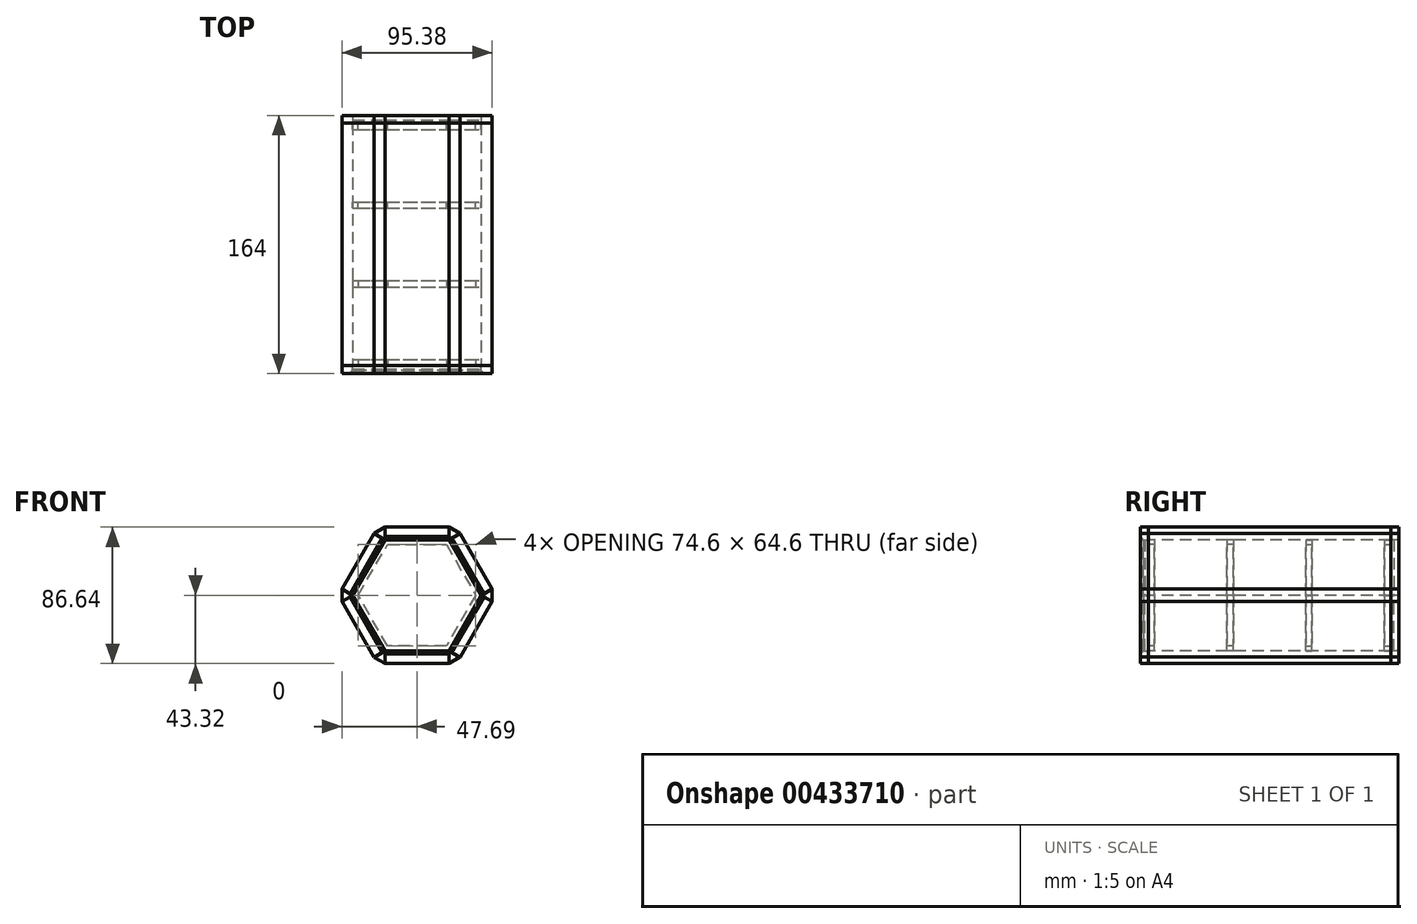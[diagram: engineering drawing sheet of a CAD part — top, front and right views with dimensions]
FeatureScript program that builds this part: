
annotation { "Feature Type Name" : "Feature", "Feature Type Description" : "" }
export const myFeature = defineFeature(function(context is Context, id is Id, definition is map)
    precondition{}
    {
        {
            var Q0;
            Q0=qCreatedBy(makeId("Front.planeOp"),FACE);
            var sketch = newSketch(context, id + "F0", { "sketchPlane" : qUnion([Q0])});
            skCircle(sketch, "E0.cCircle", {"center": v(0, 0) * mm, "radius": 43.3 * mm, "construction": true});
            skLineSegment(sketch, "E0.0", {"start": v(-50, 0) * mm, "end": v(-25, 43.3) * mm});
            skLineSegment(sketch, "E0.1", {"start": v(-25, 43.3) * mm, "end": v(25, 43.3) * mm});
            skLineSegment(sketch, "E0.2", {"start": v(25, 43.3) * mm, "end": v(50, 0) * mm});
            skLineSegment(sketch, "E0.3", {"start": v(50, 0) * mm, "end": v(25, -43.3) * mm});
            skLineSegment(sketch, "E0.4", {"start": v(25, -43.3) * mm, "end": v(-25, -43.3) * mm});
            skLineSegment(sketch, "E0.5", {"start": v(-25, -43.3) * mm, "end": v(-50, 0) * mm});
            skPoint(sketch, "E0.0.midPoint", {"position": v(-37.5, 21.65) * mm});
            skLineSegment(sketch, "E1.0", {"start": v(-20.38, 35.3) * mm, "end": v(20.38, 35.3) * mm});
            skLineSegment(sketch, "E1.1", {"start": v(40.76, 0) * mm, "end": v(20.38, -35.3) * mm});
            skLineSegment(sketch, "E1.2", {"start": v(20.38, -35.3) * mm, "end": v(-20.38, -35.3) * mm});
            skLineSegment(sketch, "E1.3", {"start": v(20.38, 35.3) * mm, "end": v(40.76, 0) * mm});
            skLineSegment(sketch, "E1.4", {"start": v(-20.38, -35.3) * mm, "end": v(-40.76, 0) * mm});
            skLineSegment(sketch, "E1.5", {"start": v(-40.76, 0) * mm, "end": v(-20.38, 35.3) * mm});
            skLineSegment(sketch, "E2.0", {"start": v(-37.3, 0) * mm, "end": v(-18.65, 32.3) * mm});
            skLineSegment(sketch, "E2.1", {"start": v(18.65, 32.3) * mm, "end": v(37.3, 0) * mm});
            skLineSegment(sketch, "E2.2", {"start": v(37.3, 0) * mm, "end": v(18.65, -32.3) * mm});
            skLineSegment(sketch, "E2.3", {"start": v(-18.65, 32.3) * mm, "end": v(18.65, 32.3) * mm});
            skLineSegment(sketch, "E2.4", {"start": v(18.65, -32.3) * mm, "end": v(-18.65, -32.3) * mm});
            skLineSegment(sketch, "E2.5", {"start": v(-18.65, -32.3) * mm, "end": v(-37.3, 0) * mm});
            skSolve(sketch);
        }
        {
            var Q0;
            Q0=makeQuery(id+"F0.imprint","IMPRINT",FACE,{"disambiguationData":[TD([[makeQuery(id+"F0.imprint","IMPRINT",EDGE,{"derivedFrom":sQuery(id+"F0.wireOp",EDGE,"E1.0")}),-1.0]])]});
            extrude(context, id + "F1", {"entities" : qUnion([Q0]), "depth" : 2 * mm});
        }
        {
            var Q0;
            Q0=makeQuery(id+"F1.opExtrude","CAP_FACE",FACE,{"disambiguationData":[OSD([sQuery(id+"F0.wireOp",EDGE,"E1.0"),sQuery(id+"F0.wireOp",EDGE,"E1.1"),sQuery(id+"F0.wireOp",EDGE,"E1.2"),sQuery(id+"F0.wireOp",EDGE,"E1.3"),sQuery(id+"F0.wireOp",EDGE,"E1.4"),sQuery(id+"F0.wireOp",EDGE,"E1.5"),sQuery(id+"F0.wireOp",EDGE,"E2.0"),sQuery(id+"F0.wireOp",EDGE,"E2.1"),sQuery(id+"F0.wireOp",EDGE,"E2.2"),sQuery(id+"F0.wireOp",EDGE,"E2.3"),sQuery(id+"F0.wireOp",EDGE,"E2.4"),sQuery(id+"F0.wireOp",EDGE,"E2.5")])],"isStart":true});
            extrude(context, id + "F2", {"entities" : qUnion([Q0]), "operationType" : NewBodyOperationType.ADD, "depth" : 2 * mm});
        }
        {
            var Q0;
            Q0=qCreatedBy(makeId("Front.planeOp"),FACE);
            cPlane(context, id + "F3", {"entities" : qUnion([Q0]), "cplaneType" : CPlaneType.OFFSET, "offset" : 50 * mm, "width" : 150 * mm, "height" : 150 * mm});
        }
        {
            var Q0;
            Q0=qCreatedBy(id+"F3.planeOp",FACE);
            cPlane(context, id + "F4", {"entities" : qUnion([Q0]), "cplaneType" : CPlaneType.OFFSET, "offset" : 50 * mm, "width" : 150 * mm, "height" : 150 * mm});
        }
        {
            var Q0;
            Q0=makeQuery(id+"F1.opExtrude","SWEPT_BODY",BODY,{"disambiguationData":[OSD([sQuery(id+"F0.wireOp",EDGE,"E1.0"),sQuery(id+"F0.wireOp",EDGE,"E1.1"),sQuery(id+"F0.wireOp",EDGE,"E1.2"),sQuery(id+"F0.wireOp",EDGE,"E1.3"),sQuery(id+"F0.wireOp",EDGE,"E1.4"),sQuery(id+"F0.wireOp",EDGE,"E1.5"),sQuery(id+"F0.wireOp",EDGE,"E2.0"),sQuery(id+"F0.wireOp",EDGE,"E2.1"),sQuery(id+"F0.wireOp",EDGE,"E2.2"),sQuery(id+"F0.wireOp",EDGE,"E2.3"),sQuery(id+"F0.wireOp",EDGE,"E2.4"),sQuery(id+"F0.wireOp",EDGE,"E2.5")])]});
            var Q1;
            Q1=qCreatedBy(id+"F3.planeOp",FACE);
            mirror(context, id + "F5", {"entities" : qUnion([Q0]), "mirrorPlane" : qUnion([Q1])});
        }
        {
            var Q0;
            Q0=qCreatedBy(id+"F3.planeOp",FACE);
            cPlane(context, id + "F6", {"entities" : qUnion([Q0]), "cplaneType" : CPlaneType.OFFSET, "offset" : 25 * mm, "width" : 150 * mm, "height" : 150 * mm});
        }
        {
            var Q0;
            Q0=makeQuery(id+"F5.opPattern","COPY",BODY,{"derivedFrom":makeQuery(id+"F1.opExtrude","SWEPT_BODY",BODY,{"disambiguationData":[OSD([sQuery(id+"F0.wireOp",EDGE,"E1.0"),sQuery(id+"F0.wireOp",EDGE,"E1.1"),sQuery(id+"F0.wireOp",EDGE,"E1.2"),sQuery(id+"F0.wireOp",EDGE,"E1.3"),sQuery(id+"F0.wireOp",EDGE,"E1.4"),sQuery(id+"F0.wireOp",EDGE,"E1.5"),sQuery(id+"F0.wireOp",EDGE,"E2.0"),sQuery(id+"F0.wireOp",EDGE,"E2.1"),sQuery(id+"F0.wireOp",EDGE,"E2.2"),sQuery(id+"F0.wireOp",EDGE,"E2.3"),sQuery(id+"F0.wireOp",EDGE,"E2.4"),sQuery(id+"F0.wireOp",EDGE,"E2.5")])]}),"instanceName":"1"});
            var Q1;
            Q1=qCreatedBy(id+"F6.planeOp",FACE);
            mirror(context, id + "F7", {"entities" : qUnion([Q0]), "mirrorPlane" : qUnion([Q1])});
        }
        {
            var Q0;
            Q0=makeQuery(id+"F7.opPattern","COPY",BODY,{"derivedFrom":makeQuery(id+"F5.opPattern","COPY",BODY,{"derivedFrom":makeQuery(id+"F1.opExtrude","SWEPT_BODY",BODY,{"disambiguationData":[OSD([sQuery(id+"F0.wireOp",EDGE,"E1.0"),sQuery(id+"F0.wireOp",EDGE,"E1.1"),sQuery(id+"F0.wireOp",EDGE,"E1.2"),sQuery(id+"F0.wireOp",EDGE,"E1.3"),sQuery(id+"F0.wireOp",EDGE,"E1.4"),sQuery(id+"F0.wireOp",EDGE,"E1.5"),sQuery(id+"F0.wireOp",EDGE,"E2.0"),sQuery(id+"F0.wireOp",EDGE,"E2.1"),sQuery(id+"F0.wireOp",EDGE,"E2.2"),sQuery(id+"F0.wireOp",EDGE,"E2.3"),sQuery(id+"F0.wireOp",EDGE,"E2.4"),sQuery(id+"F0.wireOp",EDGE,"E2.5")])]}),"instanceName":"1"}),"instanceName":"1"});
            var Q1;
            Q1=qCreatedBy(id+"F4.planeOp",FACE);
            mirror(context, id + "F8", {"entities" : qUnion([Q0]), "mirrorPlane" : qUnion([Q1])});
        }
        {
            var Q0;
            {var subQ0=sQuery(id+"F0.wireOp",EDGE,"E1.3");Q0=makeQuery(id+"F2.boolean.opBoolean","MERGE",FACE,{"derivedFrom":[makeQuery(id+"F1.opExtrude","SWEPT_FACE",FACE,{"disambiguationData":[OSD([subQ0])]}),makeQuery(id+"F2.opExtrude","SWEPT_FACE",FACE,{"disambiguationData":[OSD([subQ0])]})]});}
            cPlane(context, id + "F9", {"entities" : qUnion([Q0]), "cplaneType" : CPlaneType.OFFSET, "offset" : 0 * mm, "width" : 150 * mm, "height" : 150 * mm});
        }
        {
            var Q0;
            Q0=qCreatedBy(id+"F9.planeOp",FACE);
            var sketch = newSketch(context, id + "F10", { "sketchPlane" : qUnion([Q0])});
            skLineSegment(sketch, "E3.bottom", {"start": v(1.98, 20.38) * mm, "end": v(-152.02, 20.38) * mm});
            skLineSegment(sketch, "E3.top", {"start": v(1.98, -20.38) * mm, "end": v(-152.02, -20.38) * mm});
            skLineSegment(sketch, "E3.left", {"start": v(1.98, 20.38) * mm, "end": v(1.98, -20.38) * mm});
            skLineSegment(sketch, "E3.right", {"start": v(-152.02, 20.38) * mm, "end": v(-152.02, -20.38) * mm});
            skSolve(sketch);
        }
        {
            var Q0;
            Q0=makeQuery(id+"F10.imprint","IMPRINT",FACE,{"disambiguationData":[TD([[makeQuery(id+"F10.imprint","IMPRINT",EDGE,{"derivedFrom":sQuery(id+"F10.wireOp",EDGE,"E3.bottom")}),1.0]])]});
            extrude(context, id + "F11", {"entities" : qUnion([Q0]), "depth" : 8 * mm});
        }
        {
            var Q0;
            Q0=qCreatedBy(makeId("Top.planeOp"),FACE);
            var sketch = newSketch(context, id + "F12", { "sketchPlane" : qUnion([Q0])});
            skLineSegment(sketch, "E4", {"start": v(0, 0) * mm, "end": v(0, -129.71) * mm});
            skSolve(sketch);
        }
        {
            var Q0;
            Q0=makeQuery(id+"F11.opExtrude","SWEPT_BODY",BODY,{"disambiguationData":[OSD([sQuery(id+"F10.wireOp",EDGE,"E3.bottom"),sQuery(id+"F10.wireOp",EDGE,"E3.top"),sQuery(id+"F10.wireOp",EDGE,"E3.left"),sQuery(id+"F10.wireOp",EDGE,"E3.right")])]});
            var Q1;
            Q1=sQuery(id+"F12.wireOp",EDGE,"E4");
            circularPattern(context, id + "F13", {"entities" : qUnion([Q0]), "axis" : qUnion([Q1]), "angle" : 360 * degree, "instanceCount" : 6, "equalSpace" : true});
        }
        {
            var Q0;
            Q0=makeQuery(id+"F13.opPattern","COPY",FACE,{"derivedFrom":makeQuery(id+"F11.opExtrude","SWEPT_FACE",FACE,{"disambiguationData":[OSD([sQuery(id+"F10.wireOp",EDGE,"E3.right")])]}),"instanceName":"5"});
            var sketch = newSketch(context, id + "F14", { "sketchPlane" : qUnion([Q0])});
            skLineSegment(sketch, "E5", {"start": v(40.76, 0) * mm, "end": v(47.7, -4) * mm});
            skLineSegment(sketch, "E6", {"start": v(47.7, -4) * mm, "end": v(47.7, 4.03) * mm});
            skLineSegment(sketch, "E7", {"start": v(47.7, 4.03) * mm, "end": v(40.76, 0) * mm});
            skSolve(sketch);
        }
        {
            var Q0;
            Q0=makeQuery(id+"F14.imprint","IMPRINT",FACE,{"disambiguationData":[TD([[makeQuery(id+"F14.imprint","IMPRINT",EDGE,{"derivedFrom":sQuery(id+"F14.wireOp",EDGE,"E5")}),-1.0]])]});
            extrude(context, id + "F15", {"entities" : qUnion([Q0]), "oppositeDirection" : true, "depth" : 154 * mm});
        }
        {
            var Q0;
            Q0=makeQuery(id+"F15.opExtrude","SWEPT_BODY",BODY,{"disambiguationData":[OSD([sQuery(id+"F14.wireOp",EDGE,"E5"),sQuery(id+"F14.wireOp",EDGE,"E6"),sQuery(id+"F14.wireOp",EDGE,"E7")])]});
            var Q1;
            Q1=sQuery(id+"F12.wireOp",EDGE,"E4");
            circularPattern(context, id + "F16", {"entities" : qUnion([Q0]), "axis" : qUnion([Q1]), "angle" : 360 * degree, "instanceCount" : 6, "equalSpace" : true});
        }
        {
            var Q0;
            Q0=makeQuery(id+"F13.opPattern","COPY",FACE,{"derivedFrom":makeQuery(id+"F11.opExtrude","SWEPT_FACE",FACE,{"disambiguationData":[OSD([sQuery(id+"F10.wireOp",EDGE,"E3.left")])]}),"instanceName":"2"});
            var Q1;
            Q1=makeQuery(id+"F16.opPattern","COPY",FACE,{"derivedFrom":makeQuery(id+"F15.opExtrude","CAP_FACE",FACE,{"disambiguationData":[OSD([sQuery(id+"F14.wireOp",EDGE,"E5"),sQuery(id+"F14.wireOp",EDGE,"E6"),sQuery(id+"F14.wireOp",EDGE,"E7")])],"isStart":false}),"instanceName":"2"});
            var Q2;
            Q2=makeQuery(id+"F13.opPattern","COPY",FACE,{"derivedFrom":makeQuery(id+"F11.opExtrude","SWEPT_FACE",FACE,{"disambiguationData":[OSD([sQuery(id+"F10.wireOp",EDGE,"E3.left")])]}),"instanceName":"1"});
            var Q3;
            Q3=makeQuery(id+"F16.opPattern","COPY",FACE,{"derivedFrom":makeQuery(id+"F15.opExtrude","CAP_FACE",FACE,{"disambiguationData":[OSD([sQuery(id+"F14.wireOp",EDGE,"E5"),sQuery(id+"F14.wireOp",EDGE,"E6"),sQuery(id+"F14.wireOp",EDGE,"E7")])],"isStart":false}),"instanceName":"1"});
            var Q4;
            Q4=makeQuery(id+"F11.opExtrude","SWEPT_FACE",FACE,{"disambiguationData":[OSD([sQuery(id+"F10.wireOp",EDGE,"E3.left")])]});
            var Q5;
            Q5=makeQuery(id+"F15.opExtrude","CAP_FACE",FACE,{"disambiguationData":[OSD([sQuery(id+"F14.wireOp",EDGE,"E5"),sQuery(id+"F14.wireOp",EDGE,"E6"),sQuery(id+"F14.wireOp",EDGE,"E7")])],"isStart":false});
            var Q6;
            Q6=makeQuery(id+"F13.opPattern","COPY",FACE,{"derivedFrom":makeQuery(id+"F11.opExtrude","SWEPT_FACE",FACE,{"disambiguationData":[OSD([sQuery(id+"F10.wireOp",EDGE,"E3.left")])]}),"instanceName":"5"});
            var Q7;
            Q7=makeQuery(id+"F16.opPattern","COPY",FACE,{"derivedFrom":makeQuery(id+"F15.opExtrude","CAP_FACE",FACE,{"disambiguationData":[OSD([sQuery(id+"F14.wireOp",EDGE,"E5"),sQuery(id+"F14.wireOp",EDGE,"E6"),sQuery(id+"F14.wireOp",EDGE,"E7")])],"isStart":false}),"instanceName":"5"});
            var Q8;
            Q8=makeQuery(id+"F13.opPattern","COPY",FACE,{"derivedFrom":makeQuery(id+"F11.opExtrude","SWEPT_FACE",FACE,{"disambiguationData":[OSD([sQuery(id+"F10.wireOp",EDGE,"E3.left")])]}),"instanceName":"4"});
            var Q9;
            Q9=makeQuery(id+"F16.opPattern","COPY",FACE,{"derivedFrom":makeQuery(id+"F15.opExtrude","CAP_FACE",FACE,{"disambiguationData":[OSD([sQuery(id+"F14.wireOp",EDGE,"E5"),sQuery(id+"F14.wireOp",EDGE,"E6"),sQuery(id+"F14.wireOp",EDGE,"E7")])],"isStart":false}),"instanceName":"4"});
            var Q10;
            Q10=makeQuery(id+"F13.opPattern","COPY",FACE,{"derivedFrom":makeQuery(id+"F11.opExtrude","SWEPT_FACE",FACE,{"disambiguationData":[OSD([sQuery(id+"F10.wireOp",EDGE,"E3.left")])]}),"instanceName":"3"});
            var Q11;
            Q11=makeQuery(id+"F16.opPattern","COPY",FACE,{"derivedFrom":makeQuery(id+"F15.opExtrude","CAP_FACE",FACE,{"disambiguationData":[OSD([sQuery(id+"F14.wireOp",EDGE,"E5"),sQuery(id+"F14.wireOp",EDGE,"E6"),sQuery(id+"F14.wireOp",EDGE,"E7")])],"isStart":false}),"instanceName":"3"});
            extrude(context, id + "F17", {"entities" : qUnion([Q0, Q1, Q2, Q3, Q4, Q5, Q6, Q7, Q8, Q9, Q10, Q11]), "depth" : 5 * mm});
        }
        {
            var Q0;
            Q0=makeQuery(id+"F13.opPattern","COPY",FACE,{"derivedFrom":makeQuery(id+"F11.opExtrude","SWEPT_FACE",FACE,{"disambiguationData":[OSD([sQuery(id+"F10.wireOp",EDGE,"E3.right")])]}),"instanceName":"2"});
            var Q1;
            Q1=makeQuery(id+"F16.opPattern","COPY",FACE,{"derivedFrom":makeQuery(id+"F15.opExtrude","CAP_FACE",FACE,{"disambiguationData":[OSD([sQuery(id+"F14.wireOp",EDGE,"E5"),sQuery(id+"F14.wireOp",EDGE,"E6"),sQuery(id+"F14.wireOp",EDGE,"E7")])],"isStart":true}),"instanceName":"3"});
            var Q2;
            Q2=makeQuery(id+"F13.opPattern","COPY",FACE,{"derivedFrom":makeQuery(id+"F11.opExtrude","SWEPT_FACE",FACE,{"disambiguationData":[OSD([sQuery(id+"F10.wireOp",EDGE,"E3.right")])]}),"instanceName":"3"});
            var Q3;
            Q3=makeQuery(id+"F16.opPattern","COPY",FACE,{"derivedFrom":makeQuery(id+"F15.opExtrude","CAP_FACE",FACE,{"disambiguationData":[OSD([sQuery(id+"F14.wireOp",EDGE,"E5"),sQuery(id+"F14.wireOp",EDGE,"E6"),sQuery(id+"F14.wireOp",EDGE,"E7")])],"isStart":true}),"instanceName":"4"});
            var Q4;
            Q4=makeQuery(id+"F13.opPattern","COPY",FACE,{"derivedFrom":makeQuery(id+"F11.opExtrude","SWEPT_FACE",FACE,{"disambiguationData":[OSD([sQuery(id+"F10.wireOp",EDGE,"E3.right")])]}),"instanceName":"4"});
            var Q5;
            Q5=makeQuery(id+"F16.opPattern","COPY",FACE,{"derivedFrom":makeQuery(id+"F15.opExtrude","CAP_FACE",FACE,{"disambiguationData":[OSD([sQuery(id+"F14.wireOp",EDGE,"E5"),sQuery(id+"F14.wireOp",EDGE,"E6"),sQuery(id+"F14.wireOp",EDGE,"E7")])],"isStart":true}),"instanceName":"5"});
            var Q6;
            Q6=makeQuery(id+"F13.opPattern","COPY",FACE,{"derivedFrom":makeQuery(id+"F11.opExtrude","SWEPT_FACE",FACE,{"disambiguationData":[OSD([sQuery(id+"F10.wireOp",EDGE,"E3.right")])]}),"instanceName":"5"});
            var Q7;
            Q7=makeQuery(id+"F15.opExtrude","CAP_FACE",FACE,{"disambiguationData":[OSD([sQuery(id+"F14.wireOp",EDGE,"E5"),sQuery(id+"F14.wireOp",EDGE,"E6"),sQuery(id+"F14.wireOp",EDGE,"E7")])],"isStart":true});
            var Q8;
            Q8=makeQuery(id+"F11.opExtrude","SWEPT_FACE",FACE,{"disambiguationData":[OSD([sQuery(id+"F10.wireOp",EDGE,"E3.right")])]});
            var Q9;
            Q9=makeQuery(id+"F16.opPattern","COPY",FACE,{"derivedFrom":makeQuery(id+"F15.opExtrude","CAP_FACE",FACE,{"disambiguationData":[OSD([sQuery(id+"F14.wireOp",EDGE,"E5"),sQuery(id+"F14.wireOp",EDGE,"E6"),sQuery(id+"F14.wireOp",EDGE,"E7")])],"isStart":true}),"instanceName":"1"});
            var Q10;
            Q10=makeQuery(id+"F13.opPattern","COPY",FACE,{"derivedFrom":makeQuery(id+"F11.opExtrude","SWEPT_FACE",FACE,{"disambiguationData":[OSD([sQuery(id+"F10.wireOp",EDGE,"E3.right")])]}),"instanceName":"1"});
            var Q11;
            Q11=makeQuery(id+"F16.opPattern","COPY",FACE,{"derivedFrom":makeQuery(id+"F15.opExtrude","CAP_FACE",FACE,{"disambiguationData":[OSD([sQuery(id+"F14.wireOp",EDGE,"E5"),sQuery(id+"F14.wireOp",EDGE,"E6"),sQuery(id+"F14.wireOp",EDGE,"E7")])],"isStart":true}),"instanceName":"2"});
            extrude(context, id + "F18", {"entities" : qUnion([Q0, Q1, Q2, Q3, Q4, Q5, Q6, Q7, Q8, Q9, Q10, Q11]), "depth" : 5 * mm});
        }
        {
            var Q0;
            Q0=makeQuery(id+"F8.opPattern","COPY",FACE,{"derivedFrom":makeQuery(id+"F7.opPattern","COPY",FACE,{"derivedFrom":makeQuery(id+"F5.opPattern","COPY",FACE,{"derivedFrom":makeQuery(id+"F2.opExtrude","CAP_FACE",FACE,{"disambiguationData":[OSD([sQuery(id+"F0.wireOp",EDGE,"E1.0"),sQuery(id+"F0.wireOp",EDGE,"E1.1"),sQuery(id+"F0.wireOp",EDGE,"E1.2"),sQuery(id+"F0.wireOp",EDGE,"E1.3"),sQuery(id+"F0.wireOp",EDGE,"E1.4"),sQuery(id+"F0.wireOp",EDGE,"E1.5"),sQuery(id+"F0.wireOp",EDGE,"E2.0"),sQuery(id+"F0.wireOp",EDGE,"E2.1"),sQuery(id+"F0.wireOp",EDGE,"E2.2"),sQuery(id+"F0.wireOp",EDGE,"E2.3"),sQuery(id+"F0.wireOp",EDGE,"E2.4"),sQuery(id+"F0.wireOp",EDGE,"E2.5")])],"isStart":false}),"instanceName":"1"}),"instanceName":"1"}),"instanceName":"1"});
            var sketch = newSketch(context, id + "F19", { "sketchPlane" : qUnion([Q0])});
            skCircle(sketch, "E8.cCircle", {"center": v(0, 0) * mm, "radius": 35.3 * mm, "construction": true});
            skLineSegment(sketch, "E8.0", {"start": v(-40.76, 0) * mm, "end": v(-20.38, 35.3) * mm});
            skLineSegment(sketch, "E8.1", {"start": v(-20.38, 35.3) * mm, "end": v(20.38, 35.3) * mm});
            skLineSegment(sketch, "E8.2", {"start": v(20.38, 35.3) * mm, "end": v(40.76, 0) * mm});
            skLineSegment(sketch, "E8.3", {"start": v(40.76, 0) * mm, "end": v(20.38, -35.3) * mm});
            skLineSegment(sketch, "E8.4", {"start": v(20.38, -35.3) * mm, "end": v(-20.38, -35.3) * mm});
            skLineSegment(sketch, "E8.5", {"start": v(-20.38, -35.3) * mm, "end": v(-40.76, 0) * mm});
            skPoint(sketch, "E8.0.midPoint", {"position": v(-30.57, 17.65) * mm});
            skSolve(sketch);
        }
        {
            var Q0;
            Q0 = qSketchRegion(id + "F19", true);
            extrude(context, id + "F20", {"entities" : qUnion([Q0]), "depth" : 2 * mm});
        }
        {
            var Q0;
            Q0=makeQuery(id+"F20.opExtrude","SWEPT_BODY",BODY,{"disambiguationData":[OSD([sQuery(id+"F19.wireOp",EDGE,"E8.0"),sQuery(id+"F19.wireOp",EDGE,"E8.1"),sQuery(id+"F19.wireOp",EDGE,"E8.2"),sQuery(id+"F19.wireOp",EDGE,"E8.3"),sQuery(id+"F19.wireOp",EDGE,"E8.4"),sQuery(id+"F19.wireOp",EDGE,"E8.5")])]});
            var Q1;
            Q1=qCreatedBy(id+"F6.planeOp",FACE);
            mirror(context, id + "F21", {"entities" : qUnion([Q0]), "mirrorPlane" : qUnion([Q1])});
        }
        {
            var Q0;
            {var subQ0=sQuery(id+"F10.wireOp",EDGE,"E3.right");Q0=makeQuery(id+"F18.opExtrude","CAP_EDGE",EDGE,{"disambiguationData":[OSD([subQ0]),TDD([makeQuery(id+"F13.opPattern","COPY",EDGE,{"derivedFrom":makeQuery(id+"F11.opExtrude","CAP_EDGE",EDGE,{"disambiguationData":[OSD([subQ0])],"isStart":true}),"instanceName":"4"})])],"isStart":false});}
            chamfer(context, id + "F22", {"entities" : qUnion([Q0]), "width" : 2 * mm, "tangentPropagation" : true});
        }
        {
            var Q0;
            {var subQ0=sQuery(id+"F10.wireOp",EDGE,"E3.right");Q0=makeQuery(id+"F18.opExtrude","CAP_EDGE",EDGE,{"disambiguationData":[OSD([subQ0]),TDD([makeQuery(id+"F13.opPattern","COPY",EDGE,{"derivedFrom":makeQuery(id+"F11.opExtrude","CAP_EDGE",EDGE,{"disambiguationData":[OSD([subQ0])],"isStart":true}),"instanceName":"5"})])],"isStart":false});}
            var Q1;
            {var subQ0=sQuery(id+"F10.wireOp",EDGE,"E3.right");Q1=makeQuery(id+"F18.opExtrude","CAP_EDGE",EDGE,{"disambiguationData":[OSD([subQ0]),TDD([makeQuery(id+"F11.opExtrude","CAP_EDGE",EDGE,{"disambiguationData":[OSD([subQ0])],"isStart":true})])],"isStart":false});}
            var Q2;
            {var subQ0=sQuery(id+"F10.wireOp",EDGE,"E3.right");Q2=makeQuery(id+"F18.opExtrude","CAP_EDGE",EDGE,{"disambiguationData":[OSD([subQ0]),TDD([makeQuery(id+"F13.opPattern","COPY",EDGE,{"derivedFrom":makeQuery(id+"F11.opExtrude","CAP_EDGE",EDGE,{"disambiguationData":[OSD([subQ0])],"isStart":true}),"instanceName":"3"})])],"isStart":false});}
            var Q3;
            {var subQ0=sQuery(id+"F10.wireOp",EDGE,"E3.right");Q3=makeQuery(id+"F18.opExtrude","CAP_EDGE",EDGE,{"disambiguationData":[OSD([subQ0]),TDD([makeQuery(id+"F13.opPattern","COPY",EDGE,{"derivedFrom":makeQuery(id+"F11.opExtrude","CAP_EDGE",EDGE,{"disambiguationData":[OSD([subQ0])],"isStart":true}),"instanceName":"2"})])],"isStart":false});}
            var Q4;
            {var subQ0=sQuery(id+"F10.wireOp",EDGE,"E3.right");Q4=makeQuery(id+"F18.opExtrude","CAP_EDGE",EDGE,{"disambiguationData":[OSD([subQ0]),TDD([makeQuery(id+"F13.opPattern","COPY",EDGE,{"derivedFrom":makeQuery(id+"F11.opExtrude","CAP_EDGE",EDGE,{"disambiguationData":[OSD([subQ0])],"isStart":true}),"instanceName":"1"})])],"isStart":false});}
            chamfer(context, id + "F23", {"entities" : qUnion([Q0, Q1, Q2, Q3, Q4]), "width" : 2 * mm, "tangentPropagation" : true});
        }
    });
